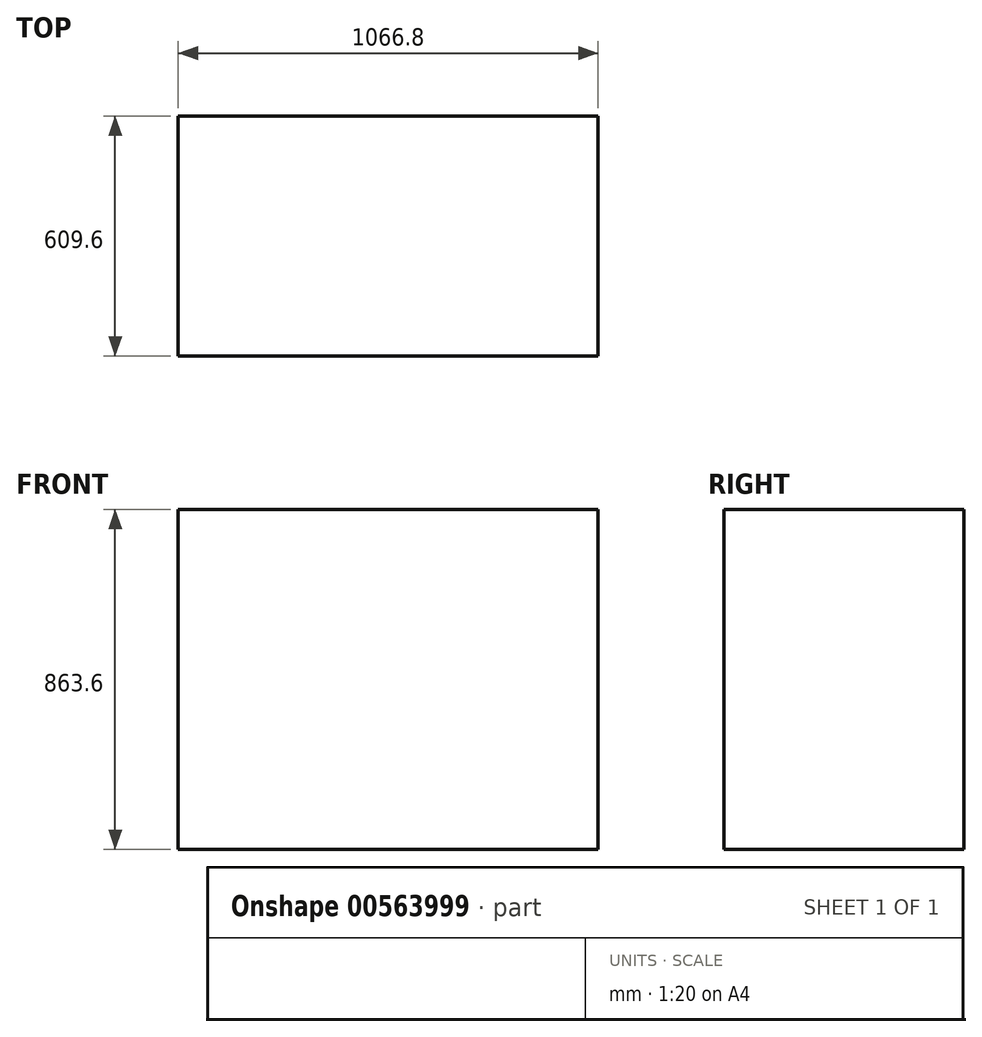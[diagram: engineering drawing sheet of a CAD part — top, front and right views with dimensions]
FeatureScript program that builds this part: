
annotation { "Feature Type Name" : "Feature", "Feature Type Description" : "" }
export const myFeature = defineFeature(function(context is Context, id is Id, definition is map)
    precondition{}
    {
        {
            var Q0;
            Q0=qCreatedBy(makeId("Front.planeOp"),FACE);
            var sketch = newSketch(context, id + "F0", { "sketchPlane" : qUnion([Q0])});
            skLineSegment(sketch, "E0.bottom", {"start": v(533.4, 431.8) * mm, "end": v(-533.4, 431.8) * mm});
            skLineSegment(sketch, "E0.top", {"start": v(533.4, -431.8) * mm, "end": v(-533.4, -431.8) * mm});
            skLineSegment(sketch, "E0.left", {"start": v(533.4, 431.8) * mm, "end": v(533.4, -431.8) * mm});
            skLineSegment(sketch, "E0.right", {"start": v(-533.4, 431.8) * mm, "end": v(-533.4, -431.8) * mm});
            skPoint(sketch, "E0.middle", {"position": v(0, 0) * mm});
            skSolve(sketch);
        }
        {
            var Q0;
            Q0 = qSketchRegion(id + "F0", true);
            extrude(context, id + "F1", {"entities" : qUnion([Q0]), "oppositeDirection" : true, "depth" : 609.6 * mm, "offsetDistance" : 25.4 * mm});
        }
        {
            var Q0;
            Q0=makeQuery(id+"F1.opExtrude","CAP_FACE",FACE,{"disambiguationData":[OSD([sQuery(id+"F0.wireOp",EDGE,"E0.bottom"),sQuery(id+"F0.wireOp",EDGE,"E0.top"),sQuery(id+"F0.wireOp",EDGE,"E0.left"),sQuery(id+"F0.wireOp",EDGE,"E0.right")])],"isStart":true});
            var sketch = newSketch(context, id + "F2", { "sketchPlane" : qUnion([Q0])});
            skLineSegment(sketch, "E1.bottom", {"start": v(609.1, 0) * mm, "end": v(533.4, 0) * mm});
            skLineSegment(sketch, "E1.top", {"start": v(609.1, -83.06) * mm, "end": v(533.4, -83.06) * mm});
            skLineSegment(sketch, "E1.left", {"start": v(609.1, 0) * mm, "end": v(609.1, -83.06) * mm});
            skLineSegment(sketch, "E1.right", {"start": v(533.4, 0) * mm, "end": v(533.4, -83.06) * mm});
            skSolve(sketch);
        }
        {
            var Q0;
            Q0=makeQuery(id+"F2.imprint","IMPRINT",FACE,{"disambiguationData":[TD([[makeQuery(id+"F2.imprint","IMPRINT",EDGE,{"derivedFrom":sQuery(id+"F2.wireOp",EDGE,"E1.bottom")}),1.0]])]});
            extrude(context, id + "F3", {"entities" : qUnion([Q0]), "depth" : 25.4 * mm, "offsetDistance" : 25.4 * mm});
        }
        {
            var Q0;
            Q0=makeQuery(id+"F3.opExtrude","SWEPT_BODY",BODY,{"disambiguationData":[OSD([sQuery(id+"F2.wireOp",EDGE,"E1.bottom"),sQuery(id+"F2.wireOp",EDGE,"E1.top"),sQuery(id+"F2.wireOp",EDGE,"E1.left"),sQuery(id+"F2.wireOp",EDGE,"E1.right")])]});
            deleteBodies(context, id + "F4", {"entities" : qUnion([Q0])});
        }
    });
